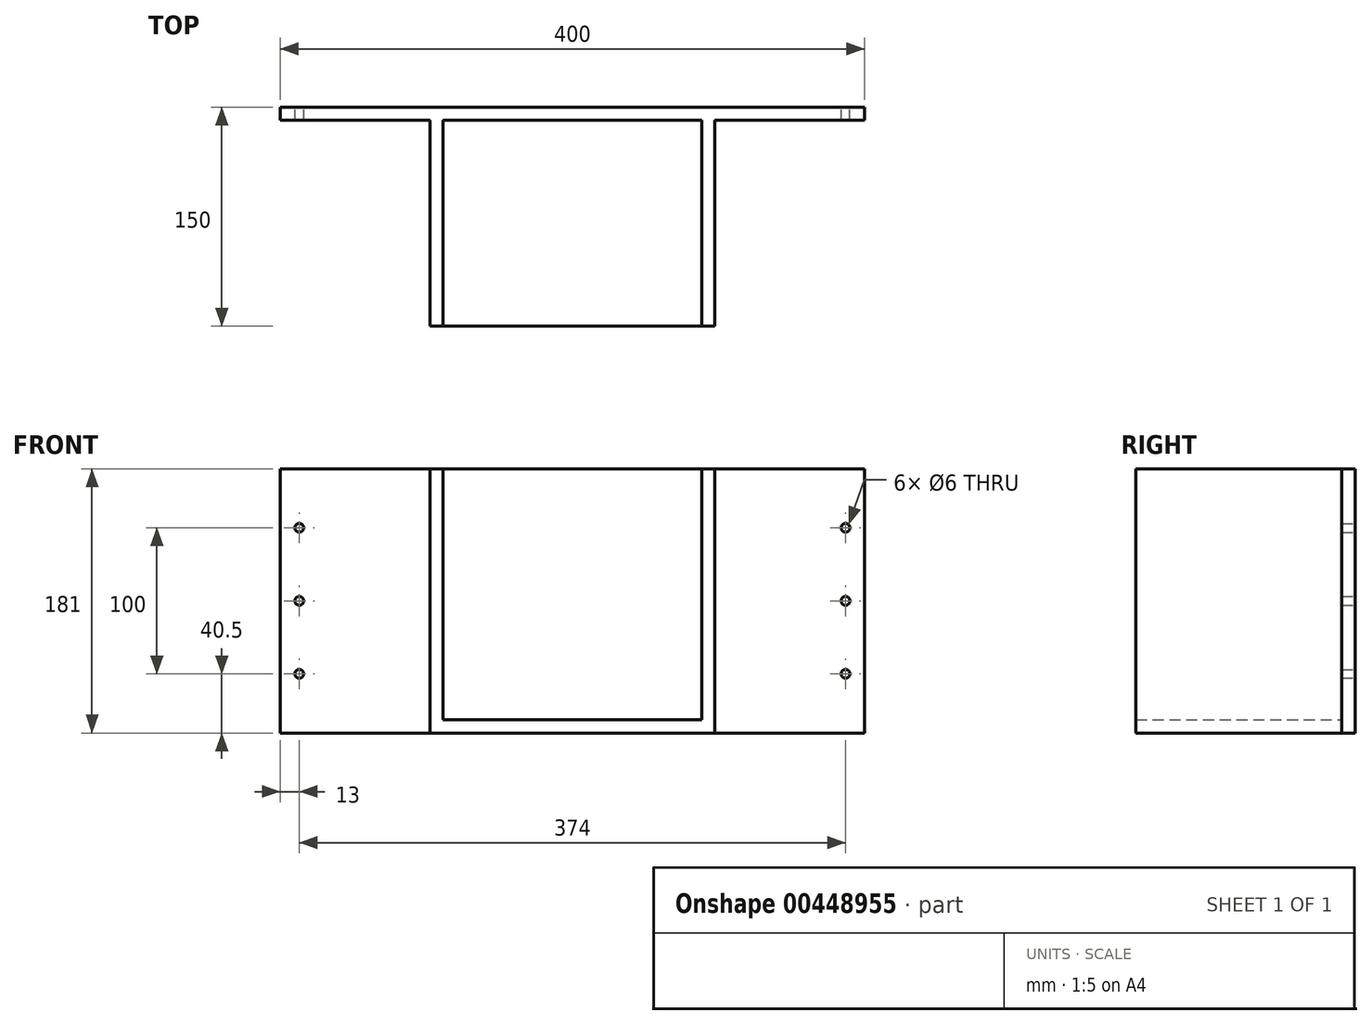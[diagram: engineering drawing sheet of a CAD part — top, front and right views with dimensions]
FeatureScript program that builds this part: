
annotation { "Feature Type Name" : "Feature", "Feature Type Description" : "" }
export const myFeature = defineFeature(function(context is Context, id is Id, definition is map)
    precondition{}
    {
        {
            var Q0;
            Q0=qCreatedBy(makeId("Front.planeOp"),FACE);
            var sketch = newSketch(context, id + "F0", { "sketchPlane" : qUnion([Q0])});
            skLineSegment(sketch, "E0.bottom", {"start": v(88.5, -4.5) * mm, "end": v(-88.5, -4.5) * mm});
            skLineSegment(sketch, "E0.top", {"start": v(88.5, 4.5) * mm, "end": v(-88.5, 4.5) * mm});
            skLineSegment(sketch, "E0.left", {"start": v(88.5, -4.5) * mm, "end": v(88.5, 4.5) * mm});
            skLineSegment(sketch, "E0.right", {"start": v(-88.5, -4.5) * mm, "end": v(-88.5, 4.5) * mm});
            skPoint(sketch, "E0.middle", {"position": v(0, 0) * mm});
            skLineSegment(sketch, "E1.bottom", {"start": v(-88.5, 4.5) * mm, "end": v(88.5, 4.5) * mm});
            skLineSegment(sketch, "E1.top", {"start": v(-88.5, 81.5) * mm, "end": v(88.5, 81.5) * mm});
            skLineSegment(sketch, "E1.left", {"start": v(-88.5, 4.5) * mm, "end": v(-88.5, 81.5) * mm});
            skLineSegment(sketch, "E1.right", {"start": v(88.5, 4.5) * mm, "end": v(88.5, 81.5) * mm});
            skLineSegment(sketch, "E2.bottom", {"start": v(-88.5, -4.5) * mm, "end": v(88.5, -4.5) * mm});
            skLineSegment(sketch, "E2.top", {"start": v(-88.5, -81.5) * mm, "end": v(88.5, -81.5) * mm});
            skLineSegment(sketch, "E2.left", {"start": v(-88.5, -4.5) * mm, "end": v(-88.5, -81.5) * mm});
            skLineSegment(sketch, "E2.right", {"start": v(88.5, -4.5) * mm, "end": v(88.5, -81.5) * mm});
            skLineSegment(sketch, "E3.bottom", {"start": v(88.5, 81.5) * mm, "end": v(-88.5, 81.5) * mm});
            skLineSegment(sketch, "E3.top", {"start": v(88.5, 90.5) * mm, "end": v(-88.5, 90.5) * mm});
            skLineSegment(sketch, "E3.left", {"start": v(88.5, 81.5) * mm, "end": v(88.5, 90.5) * mm});
            skLineSegment(sketch, "E3.right", {"start": v(-88.5, 81.5) * mm, "end": v(-88.5, 90.5) * mm});
            skLineSegment(sketch, "E4.top", {"start": v(-88.5, -90.5) * mm, "end": v(88.5, -90.5) * mm});
            skLineSegment(sketch, "E4.left", {"start": v(-88.5, -81.5) * mm, "end": v(-88.5, -90.5) * mm});
            skLineSegment(sketch, "E4.right", {"start": v(88.5, -81.5) * mm, "end": v(88.5, -90.5) * mm});
            skLineSegment(sketch, "E5.bottom", {"start": v(88.5, -90.5) * mm, "end": v(97.5, -90.5) * mm});
            skLineSegment(sketch, "E5.top", {"start": v(88.5, 90.5) * mm, "end": v(97.5, 90.5) * mm});
            skLineSegment(sketch, "E5.left", {"start": v(88.5, -90.5) * mm, "end": v(88.5, 90.5) * mm});
            skLineSegment(sketch, "E5.right", {"start": v(97.5, -90.5) * mm, "end": v(97.5, 90.5) * mm});
            skLineSegment(sketch, "E6.bottom", {"start": v(-88.5, 90.5) * mm, "end": v(-97.5, 90.5) * mm});
            skLineSegment(sketch, "E6.top", {"start": v(-88.5, -90.5) * mm, "end": v(-97.5, -90.5) * mm});
            skLineSegment(sketch, "E6.left", {"start": v(-88.5, 90.5) * mm, "end": v(-88.5, -90.5) * mm});
            skLineSegment(sketch, "E6.right", {"start": v(-97.5, 90.5) * mm, "end": v(-97.5, -90.5) * mm});
            skSolve(sketch);
        }
        {
            var Q0;
            {var subQ0=sQuery(id+"F0.wireOp",EDGE,"E1.bottom");Q0=makeQuery(id+"F0.imprint","IMPRINT",FACE,{"disambiguationData":[TD([[makeQuery(id+"F0.imprint","IMPRINT",EDGE,{"derivedFrom":subQ0}),-1.0]])]});}
            var Q1;
            {var subQ0=sQuery(id+"F0.wireOp",EDGE,"E2.top");Q1=makeQuery(id+"F0.imprint","IMPRINT",FACE,{"disambiguationData":[TD([[makeQuery(id+"F0.imprint","IMPRINT",EDGE,{"derivedFrom":subQ0}),-1.0]])]});}
            var Q2;
            {var subQ0=sQuery(id+"F0.wireOp",EDGE,"E3.bottom");Q2=makeQuery(id+"F0.imprint","IMPRINT",FACE,{"disambiguationData":[TD([[makeQuery(id+"F0.imprint","IMPRINT",EDGE,{"derivedFrom":subQ0}),-1.0]])]});}
            extrude(context, id + "F1", {"entities" : qUnion([Q0, Q1, Q2]), "depth" : 150 * mm});
        }
        {
            var Q0;
            Q0=makeQuery(id+"F1.opExtrude","CAP_FACE",FACE,{"disambiguationData":[OSD([sQuery(id+"F0.wireOp",EDGE,"E1.bottom"),sQuery(id+"F0.wireOp",EDGE,"E2.bottom"),sQuery(id+"F0.wireOp",EDGE,"E3.bottom"),sQuery(id+"F0.wireOp",EDGE,"E3.top"),sQuery(id+"F0.wireOp",EDGE,"E2.top"),sQuery(id+"F0.wireOp",EDGE,"E4.top"),sQuery(id+"F0.wireOp",EDGE,"E5.bottom"),sQuery(id+"F0.wireOp",EDGE,"E5.top"),sQuery(id+"F0.wireOp",EDGE,"E5.left"),sQuery(id+"F0.wireOp",EDGE,"E5.right"),sQuery(id+"F0.wireOp",EDGE,"E6.bottom"),sQuery(id+"F0.wireOp",EDGE,"E6.top"),sQuery(id+"F0.wireOp",EDGE,"E6.left"),sQuery(id+"F0.wireOp",EDGE,"E6.right")])],"isStart":true});
            var sketch = newSketch(context, id + "F2", { "sketchPlane" : qUnion([Q0])});
            skLineSegment(sketch, "E7.bottom", {"start": v(200, -90.5) * mm, "end": v(-200, -90.5) * mm});
            skLineSegment(sketch, "E7.top", {"start": v(200, 90.5) * mm, "end": v(-200, 90.5) * mm});
            skLineSegment(sketch, "E7.left", {"start": v(200, -90.5) * mm, "end": v(200, 90.5) * mm});
            skLineSegment(sketch, "E7.right", {"start": v(-200, -90.5) * mm, "end": v(-200, 90.5) * mm});
            skPoint(sketch, "E7.middle", {"position": v(0, 0) * mm});
            skLineSegment(sketch, "E8", {"start": v(-187, 90.5) * mm, "end": v(-187, -90.5) * mm, "construction": true});
            skCircle(sketch, "E9", {"center": v(-187, 0) * mm, "radius": 3 * mm});
            skCircle(sketch, "E10", {"center": v(-187, -50) * mm, "radius": 3 * mm});
            skCircle(sketch, "E11", {"center": v(-187, 50) * mm, "radius": 3 * mm});
            skCircle(sketch, "E12.MirrorC", {"center": v(187, 0) * mm, "radius": 3 * mm});
            skCircle(sketch, "E13.MirrorC", {"center": v(187, -50) * mm, "radius": 3 * mm});
            skCircle(sketch, "E14.MirrorC", {"center": v(187, 50) * mm, "radius": 3 * mm});
            skLineSegment(sketch, "E15.MirrorCS", {"start": v(187, 90.5) * mm, "end": v(187, -90.5) * mm, "construction": true});
            skSolve(sketch);
        }
        {
            var Q0;
            {var subQ2=sQuery(id+"F2.wireOp",EDGE,"E7.left");Q0=makeQuery(id+"F2.imprint","IMPRINT",FACE,{"disambiguationData":[TD([[makeQuery(id+"F2.imprint","IMPRINT",EDGE,{"derivedFrom":subQ2}),1.0]])]});}
            var Q1;
            {var subQ2=sQuery(id+"F2.wireOp",EDGE,"E7.right");Q1=makeQuery(id+"F2.imprint","IMPRINT",FACE,{"disambiguationData":[TD([[makeQuery(id+"F2.imprint","IMPRINT",EDGE,{"derivedFrom":subQ2}),-1.0]])]});}
            extrude(context, id + "F3", {"entities" : qUnion([Q0, Q1]), "operationType" : NewBodyOperationType.ADD, "oppositeDirection" : true, "depth" : 9 * mm});
        }
        {
            var Q0;
            {var subQ3=sQuery(id+"F0.wireOp",EDGE,"E6.bottom");Q0=makeQuery(id+"F0.imprint","IMPRINT",FACE,{"disambiguationData":[TD([[makeQuery(id+"F0.imprint","IMPRINT",EDGE,{"derivedFrom":subQ3}),1.0]])]});}
            var Q1;
            {var subQ3=sQuery(id+"F0.wireOp",EDGE,"E5.bottom");Q1=makeQuery(id+"F0.imprint","IMPRINT",FACE,{"disambiguationData":[TD([[makeQuery(id+"F0.imprint","IMPRINT",EDGE,{"derivedFrom":subQ3}),1.0]])]});}
            extrude(context, id + "F4", {"entities" : qUnion([Q0, Q1]), "operationType" : NewBodyOperationType.ADD, "depth" : 150 * mm});
        }
    });
